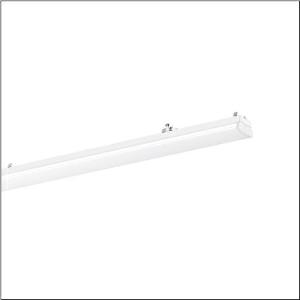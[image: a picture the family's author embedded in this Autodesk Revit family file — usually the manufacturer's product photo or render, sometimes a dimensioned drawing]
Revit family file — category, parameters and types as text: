
# Revit family: licross_r__11_recessed_opal_mo_51tl1ddn425g_3105
name_source: partatom
category: Lighting Fixtures
units: mm (PartAtom-declared; Revit-internal decimal feet)

## family parameters
Cut with Voids When Loaded = No
Host = Face
Light Source = No
Part Type = Normal
Room Calculation Point = No
Round Connector Dimension = Use Diameter
Shared = No

## types (1)
- --- (1 x LED, 2750 lm, 15.7 W, 4000K)
    Apparent Load = 16 VA
    CIE Flux Codes = 44 73 91 87 100
    Color Rendering = 80
    Color Temperature = 4000K
    Default Elevation = 1800 mm
    Description = Licross® 11 recessed opal MO, luminaire insert, of sheet steel, coil coated, white, length: 1.500mm, width: 76mm, height: 87mm, LED rated luminous flux: 2.750lm, light colour: 840, control gear: DALI 2, with plug, 5-pole, with phase selection, mains connection: 220..240V, AC, 50/60Hz, rated input power: 16W, halogen-free wiring, primary optical cover: cover, of PMMA, light emission: direct with ceiling illumination distribution, primary light characteristic: symmetric, protection rating (complete): IP40, insulation class (complete): insulation class I (protective earthing), certification: CE, ENEC, VDE, UKCA, protection symbol: D if used in an environment without relevant dust loads with corresponding accessories, impact resistance: IK06, permissible ambient temperature for indoor applications: -25..+50°C, corresponds to IFS (International Featured Standards) requirements for safety and quality in the food industry, reducing of maximum allowable ambient temperature of 5°C with ceiling mounting, LABS conformity tested according to VDMA 24364:2018-05, packaging unit: 1 piece
    Height = 83 mm
    Lamp = 1 x LED
    Lamp Light Flux = 2750 lm
    Lamp Power = 15.7 W
    Lamp count = 1
    Length = 1500 mm
    Luminous efficacy = 175 lm/W
    Manufacturer = Siteco
    ModVariant = No
    Model = 51TL1DDN425G
    Mounting Place = Ceiling
    Mounting Type = Pendant
    Number of Poles = 1
    OnlyDefault = Yes
    Power Factor = 1
    Product Name = Licross® 11 recessed opal MO
    Product group = luminaire insert
    ProductGroupID = 901
    Protection Class = Protection class I
    Protection Degree = IP 40
    RLX_Detail_Level = 1
    RLX_Emergency_Light_Flux = 0 lm
    RLX_Emergency_Type = 0
    RLX_Emergency_Type_DB = No
    RlxData = <blob elided: 17645 chars, md5=7aca7018>
    Socket = socket
    Standby Power = 0 W
    System Light Flux = 2750 lm
    System Power = 16 W
    Type Comments = factory setting: luminous flux: 100 % | dim-lin: 254 | 101 mA
    Type Image = l_1313666.jpg
    URL = http://relux.com
    VarID = @adj_027509
    Voltage = 0 V
    Weight = 0.00 kg
    Width = 76 mm

## geometry (parser evidence)
native form markers: Blend x4, Sweep x12
no freeform markers — native parametric forms only
